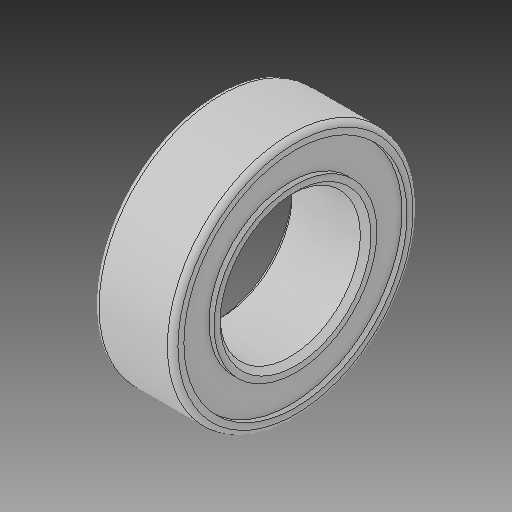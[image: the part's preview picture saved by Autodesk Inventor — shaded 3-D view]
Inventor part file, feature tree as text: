
AUTODESK INVENTOR PART (.ipt)
format: ipt  version: 2017 (Build 210142000, 142)  size: 183,808 bytes
history: native  units: in
note: dims shown in document units (in); Inventor stores cm internally (conversion verified against a paired STEP export)
features: revolve x1
ambient origin geometry x8: Origin, YZ Plane, XZ Plane, XY Plane, X Axis, Y Axis, Z Axis, Center Point
bodies: Solid1 (feature_tree)
feature tree (1):
  revolve  "Revolve1"  [1 undecoded]
note: 1 required parameter value undecoded (feature->parameter linkage not recoverable at this tier; creation-order binding heuristic only, values carry confidence <= 0.55)
